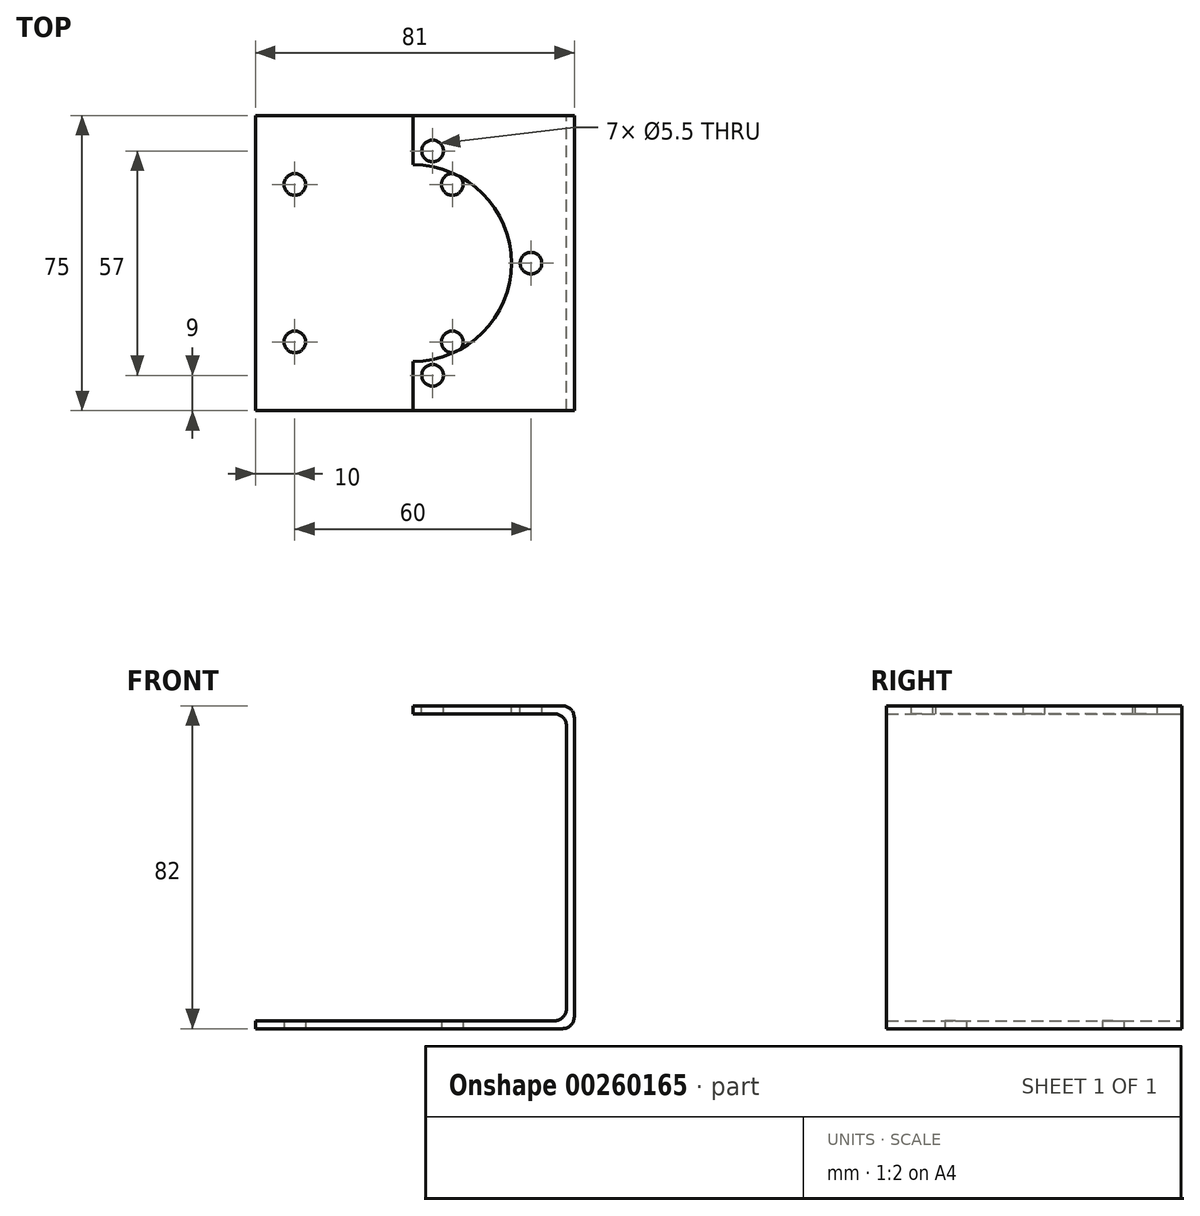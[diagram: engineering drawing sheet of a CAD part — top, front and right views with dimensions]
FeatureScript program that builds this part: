
annotation { "Feature Type Name" : "Feature", "Feature Type Description" : "" }
export const myFeature = defineFeature(function(context is Context, id is Id, definition is map)
    precondition{}
    {
        {
            var Q0;
            Q0=qCreatedBy(makeId("Front.planeOp"),FACE);
            var sketch = newSketch(context, id + "F0", { "sketchPlane" : qUnion([Q0])});
            skLineSegment(sketch, "E0", {"start": v(-80, 0) * mm, "end": v(0, 0) * mm});
            skLineSegment(sketch, "E1", {"start": v(0, 0) * mm, "end": v(0, 80) * mm});
            skLineSegment(sketch, "E2", {"start": v(0, 80) * mm, "end": v(-40, 80) * mm});
            skSolve(sketch);
        }
        {
            var Q0;
            Q0=sQuery(id+"F0.wireOp",VERTEX,"E0.start");
            var Q1;
            Q1=sQuery(id+"F0.wireOp",EDGE,"E0");
            cPlane(context, id + "F1", {"entities" : qUnion([Q0, Q1]), "cplaneType" : CPlaneType.LINE_POINT, "offset" : 25 * mm, "width" : 150 * mm, "height" : 150 * mm});
        }
        {
            var Q0;
            Q0=qCreatedBy(id+"F1.planeOp",FACE);
            var sketch = newSketch(context, id + "F2", { "sketchPlane" : qUnion([Q0])});
            skLineSegment(sketch, "E3.bottom", {"start": v(-37.5, -1) * mm, "end": v(37.5, -1) * mm});
            skLineSegment(sketch, "E3.top", {"start": v(-37.5, 1) * mm, "end": v(37.5, 1) * mm});
            skLineSegment(sketch, "E3.left", {"start": v(-37.5, -1) * mm, "end": v(-37.5, 1) * mm});
            skLineSegment(sketch, "E3.right", {"start": v(37.5, -1) * mm, "end": v(37.5, 1) * mm});
            skPoint(sketch, "E3.middle", {"position": v(0, 0) * mm});
            skSolve(sketch);
        }
        {
            var Q0;
            Q0=makeQuery(id+"F2.imprint","IMPRINT",FACE,{"disambiguationData":[TD([[makeQuery(id+"F2.imprint","IMPRINT",EDGE,{"derivedFrom":sQuery(id+"F2.wireOp",EDGE,"E3.bottom")}),1.0]])]});
            var Q1;
            Q1=sQuery(id+"F0.wireOp",EDGE,"E0");
            var Q2;
            Q2=sQuery(id+"F0.wireOp",EDGE,"E1");
            var Q3;
            Q3=sQuery(id+"F0.wireOp",EDGE,"E2");
            sweep(context, id + "F3", {"profiles" : qUnion([Q0]), "path" : qUnion([Q1, Q2, Q3])});
        }
        {
            var Q0;
            Q0=makeQuery(id+"F3.opSweep","MID_CAP_EDGE",EDGE,{"disambiguationData":[OSD([sQuery(id+"F0.wireOp",VERTEX,"E1.start"),sQuery(id+"F2.wireOp",EDGE,"E3.top")])],"capPos":1.0});
            var Q1;
            Q1=makeQuery(id+"F3.opSweep","MID_CAP_EDGE",EDGE,{"disambiguationData":[OSD([sQuery(id+"F0.wireOp",VERTEX,"E2.start"),sQuery(id+"F2.wireOp",EDGE,"E3.top")])],"capPos":2.0});
            var Q2;
            Q2=makeQuery(id+"F3.opSweep","MID_CAP_EDGE",EDGE,{"disambiguationData":[OSD([sQuery(id+"F0.wireOp",VERTEX,"E1.start"),sQuery(id+"F2.wireOp",EDGE,"E3.bottom")])],"capPos":1.0});
            var Q3;
            Q3=makeQuery(id+"F3.opSweep","MID_CAP_EDGE",EDGE,{"disambiguationData":[OSD([sQuery(id+"F0.wireOp",VERTEX,"E2.start"),sQuery(id+"F2.wireOp",EDGE,"E3.bottom")])],"capPos":2.0});
            fillet(context, id + "F4", {"entities" : qUnion([Q0, Q1, Q2, Q3]), "radius" : 3 * mm, "tangentPropagation" : true, "allowEdgeOverflow" : false});
        }
        {
            var Q0;
            Q0=makeQuery(id+"F3.opSweep","SWEPT_FACE",FACE,{"disambiguationData":[OSD([sQuery(id+"F0.wireOp",EDGE,"E2"),sQuery(id+"F2.wireOp",EDGE,"E3.bottom")])]});
            var sketch = newSketch(context, id + "F5", { "sketchPlane" : qUnion([Q0])});
            skCircle(sketch, "E4", {"center": v(-40, 0) * mm, "radius": 25 * mm});
            skSolve(sketch);
        }
        {
            var Q0;
            {var subQ0=sQuery(id+"F5.wireOp",EDGE,"E4");var subQ1=makeQuery(id+"F3.opSweep","CAP_EDGE",EDGE,{"disambiguationData":[OSD([sQuery(id+"F0.wireOp",VERTEX,"E2.end"),sQuery(id+"F2.wireOp",EDGE,"E3.bottom")])],"isStart":false});var subQ2=makeQuery(id+"F5.imprint","INTERSECT",VERTEX,{"disambiguationData":[OD(0.0)],"derivedFrom":[subQ1,subQ0]});Q0=makeQuery(id+"F5.imprint","IMPRINT",FACE,{"disambiguationData":[TD([[makeQuery(id+"F5.imprint","IMPRINT",EDGE,{"disambiguationData":[TD([[subQ2,-1.0]])],"derivedFrom":subQ0}),1.0]])]});}
            extrude(context, id + "F6", {"entities" : qUnion([Q0]), "operationType" : NewBodyOperationType.REMOVE, "endBound" : BoundingType.UP_TO_NEXT, "oppositeDirection" : true, "depth" : 25 * mm});
        }
        {
            var Q0;
            Q0=makeQuery(id+"F3.opSweep","SWEPT_FACE",FACE,{"disambiguationData":[OSD([sQuery(id+"F0.wireOp",EDGE,"E0"),sQuery(id+"F2.wireOp",EDGE,"E3.bottom")])]});
            var sketch = newSketch(context, id + "F7", { "sketchPlane" : qUnion([Q0])});
            skPoint(sketch, "E5", {"position": v(-70, 20) * mm});
            skPoint(sketch, "E6", {"position": v(-70, -20) * mm});
            skPoint(sketch, "E7", {"position": v(-30, -20) * mm});
            skPoint(sketch, "E8", {"position": v(-30, 20) * mm});
            skSolve(sketch);
        }
        {
            var Q0;
            Q0=makeQuery(id+"F3.opSweep","SWEPT_FACE",FACE,{"disambiguationData":[OSD([sQuery(id+"F0.wireOp",EDGE,"E2"),sQuery(id+"F2.wireOp",EDGE,"E3.bottom")])]});
            var sketch = newSketch(context, id + "F8", { "sketchPlane" : qUnion([Q0])});
            skPoint(sketch, "E9", {"position": v(-10, 0) * mm});
            skPoint(sketch, "E9.positionSnap0", {"position": v(-15, 0) * mm});
            skPoint(sketch, "E10", {"position": v(-35, -28.5) * mm});
            skPoint(sketch, "E10.positionSnap0", {"position": v(-40, -28.5) * mm});
            skPoint(sketch, "E11", {"position": v(-35, 28.5) * mm});
            skPoint(sketch, "E11.positionSnap0", {"position": v(-40, 28.5) * mm});
            skSolve(sketch);
        }
        {
            var Q0;
            Q0=sQuery(id+"F8.wireOp",VERTEX,"E11");
            var Q1;
            Q1=sQuery(id+"F8.wireOp",VERTEX,"E9");
            var Q2;
            Q2=sQuery(id+"F8.wireOp",VERTEX,"E10");
            var Q3;
            Q3=sQuery(id+"F7.wireOp",VERTEX,"E8");
            var Q4;
            Q4=sQuery(id+"F7.wireOp",VERTEX,"E7");
            var Q5;
            Q5=sQuery(id+"F7.wireOp",VERTEX,"E6");
            var Q6;
            Q6=sQuery(id+"F7.wireOp",VERTEX,"E5");
            var Q7;
            Q7=makeQuery(id+"F3.opSweep","SWEPT_BODY",BODY,{"disambiguationData":[OSD([sQuery(id+"F0.wireOp",EDGE,"E2"),sQuery(id+"F2.wireOp",EDGE,"E3.bottom"),sQuery(id+"F2.wireOp",EDGE,"E3.top"),sQuery(id+"F2.wireOp",EDGE,"E3.left"),sQuery(id+"F2.wireOp",EDGE,"E3.right")])]});
            hole(context, id + "F9", {"style" : HoleStyle.SIMPLE, "endStyle" : HoleEndStyle.BLIND, "holeDiameter" : 5.5 * mm, "holeDepth" : 18 * mm, "tappedDepth" : 32 * mm, "tapClearance" : 3, "startFromSketch" : true, "locations" : qUnion([Q0, Q1, Q2, Q3, Q4, Q5, Q6]), "scope" : qUnion([Q7])});
        }
    });
